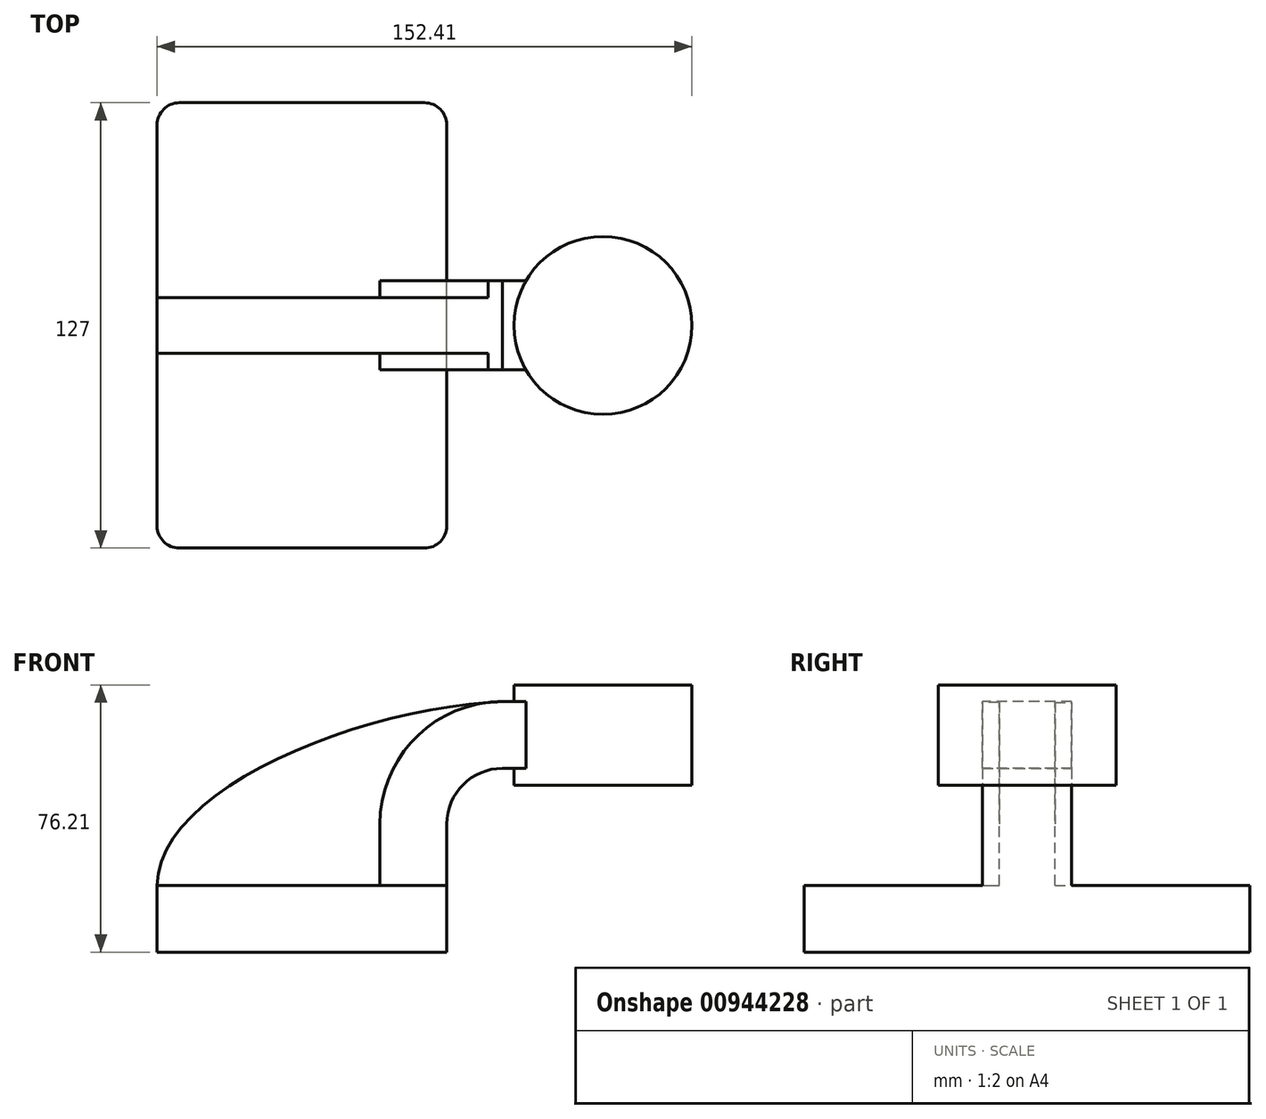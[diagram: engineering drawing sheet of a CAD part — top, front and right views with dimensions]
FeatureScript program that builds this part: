
annotation { "Feature Type Name" : "Feature", "Feature Type Description" : "" }
export const myFeature = defineFeature(function(context is Context, id is Id, definition is map)
    precondition{}
    {
        {
            var Q0;
            Q0=qCreatedBy(makeId("Front.planeOp"),FACE);
            var sketch = newSketch(context, id + "F0", { "sketchPlane" : qUnion([Q0])});
            skLineSegment(sketch, "E0.bottom", {"start": v(-41.28, 9.52) * mm, "end": v(41.28, 9.53) * mm});
            skLineSegment(sketch, "E0.top", {"start": v(-41.28, -9.53) * mm, "end": v(41.28, -9.53) * mm});
            skLineSegment(sketch, "E0.left", {"start": v(-41.28, 9.52) * mm, "end": v(-41.27, -9.53) * mm});
            skLineSegment(sketch, "E0.right", {"start": v(41.28, 9.53) * mm, "end": v(41.28, -9.52) * mm});
            skPoint(sketch, "E0.middle", {"position": v(0, 0) * mm});
            skLineSegment(sketch, "E1.bottom", {"start": v(60.32, 38.1) * mm, "end": v(111.12, 38.1) * mm});
            skLineSegment(sketch, "E1.top", {"start": v(60.32, 66.67) * mm, "end": v(111.12, 66.67) * mm});
            skLineSegment(sketch, "E1.left", {"start": v(60.32, 38.1) * mm, "end": v(60.32, 42.88) * mm});
            skLineSegment(sketch, "E1.right", {"start": v(111.12, 38.1) * mm, "end": v(111.12, 66.67) * mm});
            skPoint(sketch, "E1.middle", {"position": v(85.72, 52.39) * mm});
            skLineSegment(sketch, "E2", {"start": v(41.27, 9.53) * mm, "end": v(41.27, 27) * mm});
            skArc(sketch, "E3", {"start": v(41.27, 27) * mm, "mid": v(45.92, 38.23) * mm, "end": v(57.15, 42.88) * mm});
            skLineSegment(sketch, "E4", {"start": v(57.15, 42.88) * mm, "end": v(85.76, 42.88) * mm});
            skLineSegment(sketch, "E5.0", {"start": v(57.15, 61.93) * mm, "end": v(60.32, 61.93) * mm});
            skArc(sketch, "E5.1", {"start": v(22.22, 27) * mm, "mid": v(32.45, 51.7) * mm, "end": v(57.15, 61.93) * mm});
            skLineSegment(sketch, "E5.2", {"start": v(22.22, 9.53) * mm, "end": v(22.22, 27) * mm});
            skPoint(sketch, "E6.startSnap0", {"position": v(85.72, 38.1) * mm});
            skFitSpline(sketch, "E7", {"points": [v(-41.28, 9.52) * mm, v(57.15, 61.93) * mm], "startDerivative": vector(0.77, 81.93) * mm, "endDerivative": vector(124.92, 5.33) * mm});
            skLineSegment(sketch, "E8", {"start": v(60.32, 61.93) * mm, "end": v(85.76, 61.93) * mm});
            skLineSegment(sketch, "E9", {"start": v(60.32, 42.88) * mm, "end": v(60.32, 66.67) * mm});
            skPoint(sketch, "E10", {"position": v(85.76, 38.1) * mm});
            skLineSegment(sketch, "E11", {"start": v(85.76, 38.1) * mm, "end": v(85.76, 42.88) * mm});
            skLineSegment(sketch, "E12", {"start": v(85.76, 61.93) * mm, "end": v(85.76, 42.88) * mm});
            skLineSegment(sketch, "E13", {"start": v(85.76, 61.93) * mm, "end": v(85.76, 66.68) * mm});
            skSolve(sketch);
        }
        {
            var Q0;
            Q0=makeQuery(id+"F0.imprint","IMPRINT",FACE,{"disambiguationData":[TD([[makeQuery(id+"F0.imprint","IMPRINT",EDGE,{"derivedFrom":sQuery(id+"F0.wireOp",EDGE,"E0.top")}),1.0]])]});
            extrude(context, id + "F1", {"entities" : qUnion([Q0]), "endBound" : BoundingType.SYMMETRIC, "depth" : 127 * mm, "offsetDistance" : 25.4 * mm});
        }
        {
            var Q0;
            {var subQ4=sQuery(id+"F0.wireOp",EDGE,"E2");Q0=makeQuery(id+"F0.imprint","IMPRINT",FACE,{"disambiguationData":[TD([[makeQuery(id+"F0.imprint","IMPRINT",EDGE,{"derivedFrom":subQ4}),1.0]])]});}
            var Q1;
            {var subQ4=sQuery(id+"F0.wireOp",EDGE,"E8");Q1=makeQuery(id+"F0.imprint","IMPRINT",FACE,{"disambiguationData":[TD([[makeQuery(id+"F0.imprint","IMPRINT",EDGE,{"derivedFrom":subQ4}),-1.0]])]});}
            extrude(context, id + "F2", {"entities" : qUnion([Q0, Q1]), "operationType" : NewBodyOperationType.ADD, "endBound" : BoundingType.SYMMETRIC, "depth" : 25.4 * mm, "offsetDistance" : 25.4 * mm});
        }
        {
            var Q0;
            {var subQ3=sQuery(id+"F0.wireOp",EDGE,"E5.2");Q0=makeQuery(id+"F0.imprint","IMPRINT",FACE,{"disambiguationData":[TD([[makeQuery(id+"F0.imprint","IMPRINT",EDGE,{"derivedFrom":subQ3}),1.0]])]});}
            extrude(context, id + "F3", {"entities" : qUnion([Q0]), "operationType" : NewBodyOperationType.ADD, "endBound" : BoundingType.SYMMETRIC, "depth" : 15.88 * mm, "offsetDistance" : 25.4 * mm});
        }
        {
            var Q0;
            {var subQ1=sQuery(id+"F0.wireOp",EDGE,"E1.right");Q0=makeQuery(id+"F0.imprint","IMPRINT",FACE,{"disambiguationData":[TD([[makeQuery(id+"F0.imprint","IMPRINT",EDGE,{"derivedFrom":subQ1}),1.0]])]});}
            var Q1;
            Q1=sQuery(id+"F0.wireOp",EDGE,"E12");
            revolve(context, id + "F4", {"operationType" : NewBodyOperationType.ADD, "surfaceOperationType" : NewSurfaceOperationType.NEW, "entities" : qUnion([Q0]), "axis" : qUnion([Q1]), "revolveType" : RevolveType.FULL});
        }
        {
            var Q0;
            Q0=makeQuery(id+"F1.opExtrude","CAP_EDGE",EDGE,{"disambiguationData":[OSD([sQuery(id+"F0.wireOp",EDGE,"E0.right")])],"isStart":false});
            var Q1;
            Q1=makeQuery(id+"F1.opExtrude","CAP_EDGE",EDGE,{"disambiguationData":[OSD([sQuery(id+"F0.wireOp",EDGE,"E0.left")])],"isStart":false});
            var Q2;
            Q2=makeQuery(id+"F1.opExtrude","CAP_EDGE",EDGE,{"disambiguationData":[OSD([sQuery(id+"F0.wireOp",EDGE,"E0.right")])],"isStart":true});
            var Q3;
            Q3=makeQuery(id+"F1.opExtrude","CAP_EDGE",EDGE,{"disambiguationData":[OSD([sQuery(id+"F0.wireOp",EDGE,"E0.left")])],"isStart":true});
            fillet(context, id + "F5", {"entities" : qUnion([Q0, Q1, Q2, Q3]), "radius" : 6.35 * mm, "tangentPropagation" : true, "allowEdgeOverflow" : false});
        }
    });
